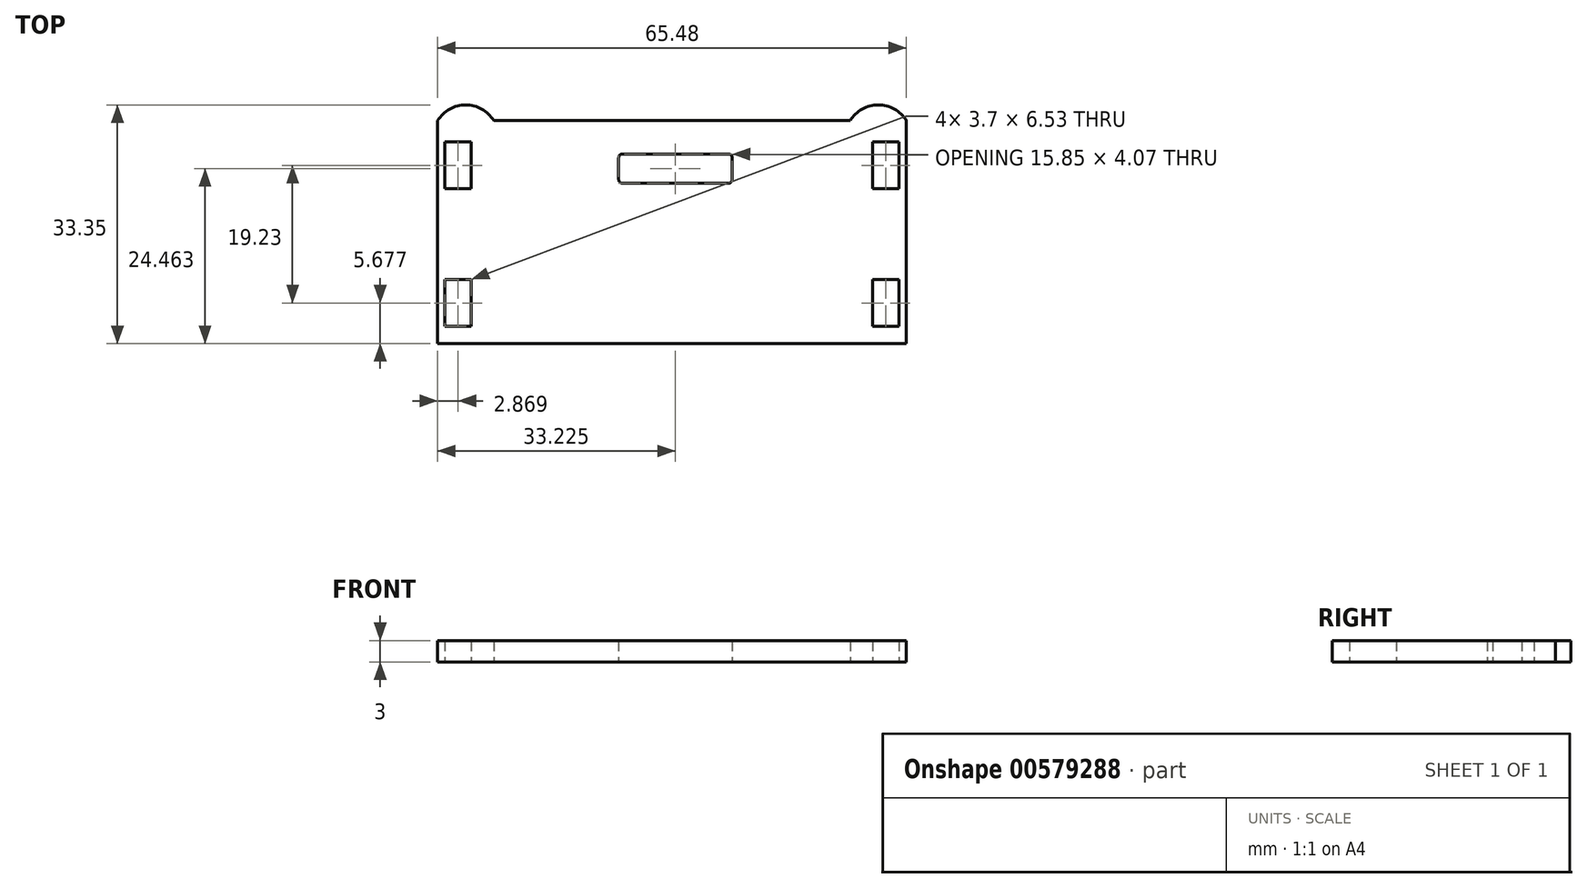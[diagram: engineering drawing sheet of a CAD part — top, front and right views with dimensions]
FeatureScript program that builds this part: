
annotation { "Feature Type Name" : "Feature", "Feature Type Description" : "" }
export const myFeature = defineFeature(function(context is Context, id is Id, definition is map)
    precondition{}
    {
        {
            var Q0;
            Q0=qCreatedBy(makeId("Top.planeOp"),FACE);
            var sketch = newSketch(context, id + "F0", { "sketchPlane" : qUnion([Q0])});
            skLineSegment(sketch, "E0.top", {"start": v(-32.14, -18.06) * mm, "end": v(33.44, -18.06) * mm});
            skLineSegment(sketch, "E0.left", {"start": v(-32.14, 13.11) * mm, "end": v(-32.14, -18.06) * mm});
            skArc(sketch, "E1", {"start": v(-24.29, 13.11) * mm, "mid": v(-28.21, 15.3) * mm, "end": v(-32.14, 13.11) * mm});
            skPoint(sketch, "E2.end.orphan", {"position": v(-28.21, 15.3) * mm});
            skPoint(sketch, "E3.start.orphan", {"position": v(-28.21, 13.11) * mm});
            skLineSegment(sketch, "E4.bottom", {"start": v(-31.12, -9.12) * mm, "end": v(-27.42, -9.12) * mm});
            skLineSegment(sketch, "E4.top", {"start": v(-31.12, -15.65) * mm, "end": v(-27.42, -15.65) * mm});
            skLineSegment(sketch, "E4.left", {"start": v(-31.12, -9.12) * mm, "end": v(-31.12, -15.65) * mm});
            skLineSegment(sketch, "E4.right", {"start": v(-27.42, -9.12) * mm, "end": v(-27.42, -15.65) * mm});
            skLineSegment(sketch, "E5.bottom", {"start": v(-31.12, 10.11) * mm, "end": v(-27.42, 10.11) * mm});
            skLineSegment(sketch, "E5.top", {"start": v(-31.12, 3.58) * mm, "end": v(-27.42, 3.58) * mm});
            skLineSegment(sketch, "E5.left", {"start": v(-31.12, 10.11) * mm, "end": v(-31.12, 3.58) * mm});
            skLineSegment(sketch, "E5.right", {"start": v(-27.42, 10.11) * mm, "end": v(-27.42, 3.58) * mm});
            skPoint(sketch, "E6.MirrorP", {"position": v(29.42, 13.11) * mm});
            skArc(sketch, "E7.MirrorCS", {"start": v(25.5, 13.11) * mm, "mid": v(29.42, 15.3) * mm, "end": v(33.34, 13.11) * mm});
            skPoint(sketch, "E8.MirrorP", {"position": v(29.42, 15.3) * mm});
            skLineSegment(sketch, "E9.MirrorCS", {"start": v(33.34, 13.11) * mm, "end": v(33.34, -18.06) * mm});
            skLineSegment(sketch, "E10", {"start": v(-24.29, 13.11) * mm, "end": v(25.5, 13.11) * mm});
            skLineSegment(sketch, "E11.MirrorCS", {"start": v(28.63, -9.12) * mm, "end": v(28.63, -15.65) * mm});
            skLineSegment(sketch, "E12.MirrorCS", {"start": v(32.33, 10.11) * mm, "end": v(28.63, 10.11) * mm});
            skLineSegment(sketch, "E13.MirrorCS", {"start": v(32.33, -15.65) * mm, "end": v(28.63, -15.65) * mm});
            skLineSegment(sketch, "E14.MirrorCS", {"start": v(32.33, -9.12) * mm, "end": v(32.33, -15.65) * mm});
            skLineSegment(sketch, "E15.MirrorCS", {"start": v(32.33, 3.58) * mm, "end": v(28.63, 3.58) * mm});
            skLineSegment(sketch, "E16.MirrorCS", {"start": v(32.33, -9.12) * mm, "end": v(28.63, -9.12) * mm});
            skLineSegment(sketch, "E17.MirrorCS", {"start": v(32.33, 10.11) * mm, "end": v(32.33, 3.58) * mm});
            skLineSegment(sketch, "E18.MirrorCS", {"start": v(28.63, 10.11) * mm, "end": v(28.63, 3.58) * mm});
            skLineSegment(sketch, "E19.bottom", {"start": v(-6.34, 8.44) * mm, "end": v(8.5, 8.44) * mm});
            skLineSegment(sketch, "E19.top", {"start": v(-6.34, 4.37) * mm, "end": v(8.5, 4.37) * mm});
            skLineSegment(sketch, "E19.left", {"start": v(-6.84, 7.94) * mm, "end": v(-6.84, 4.87) * mm});
            skLineSegment(sketch, "E19.right", {"start": v(9, 7.94) * mm, "end": v(9, 4.87) * mm});
            skArc(sketch, "E20", {"start": v(9, 7.94) * mm, "mid": v(8.86, 8.3) * mm, "end": v(8.5, 8.44) * mm});
            skArc(sketch, "E21", {"start": v(8.5, 4.37) * mm, "mid": v(8.86, 4.51) * mm, "end": v(9, 4.87) * mm});
            skPoint(sketch, "E22.orphan", {"position": v(9, 8.44) * mm});
            skPoint(sketch, "E23.start.orphan", {"position": v(9, 4.37) * mm});
            skLineSegment(sketch, "E24.MirrorCS", {"start": v(8.5, 8.44) * mm, "end": v(-6.34, 8.44) * mm});
            skLineSegment(sketch, "E25.MirrorCS", {"start": v(8.5, 4.37) * mm, "end": v(-6.34, 4.37) * mm});
            skArc(sketch, "E26.MirrorCS", {"start": v(-6.84, 7.94) * mm, "mid": v(-6.7, 8.3) * mm, "end": v(-6.34, 8.44) * mm});
            skArc(sketch, "E27.MirrorCS", {"start": v(-6.34, 4.37) * mm, "mid": v(-6.7, 4.51) * mm, "end": v(-6.84, 4.87) * mm});
            skPoint(sketch, "E28.MirrorP", {"position": v(-6.05, 5.74) * mm});
            skPoint(sketch, "E29.MirrorP", {"position": v(-6.05, 1.67) * mm});
            skPoint(sketch, "E30.orphan", {"position": v(-6.84, 8.44) * mm});
            skPoint(sketch, "E31.orphan", {"position": v(-6.84, 4.37) * mm});
            skSolve(sketch);
        }
        {
            var Q0;
            {var subQ1=sQuery(id+"F0.wireOp",EDGE,"E0.left");Q0=makeQuery(id+"F0.imprint","IMPRINT",FACE,{"disambiguationData":[TD([[makeQuery(id+"F0.imprint","IMPRINT",EDGE,{"derivedFrom":subQ1}),1.0]])]});}
            extrude(context, id + "F1", {"entities" : qUnion([Q0]), "depth" : 3 * mm, "offsetDistance" : 25.4 * mm});
        }
    });
